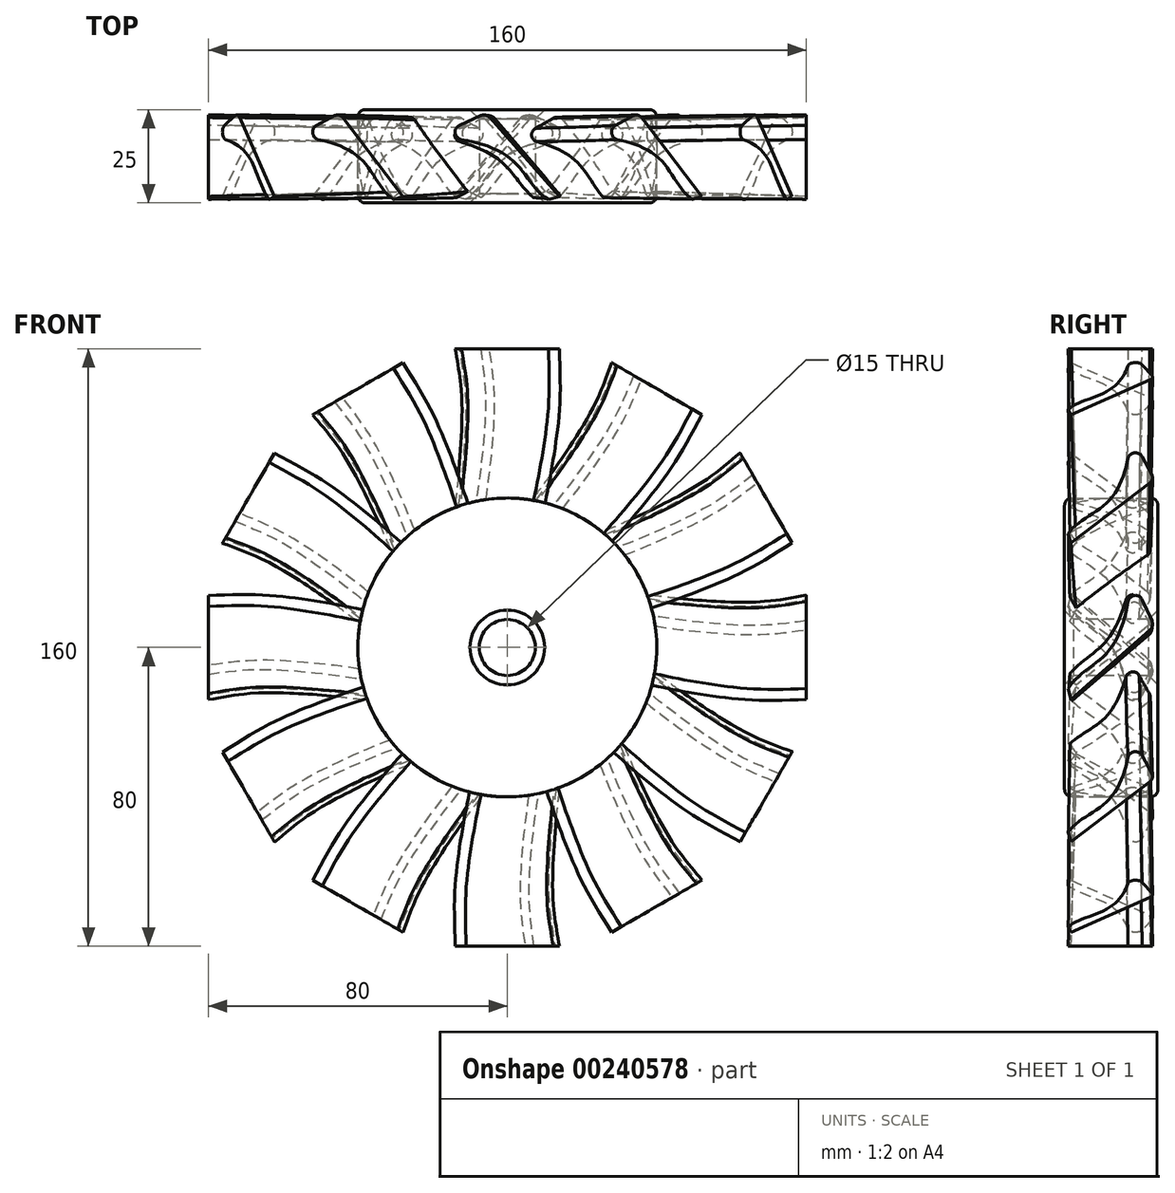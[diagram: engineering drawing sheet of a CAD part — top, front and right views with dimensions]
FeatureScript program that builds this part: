
annotation { "Feature Type Name" : "Feature", "Feature Type Description" : "" }
export const myFeature = defineFeature(function(context is Context, id is Id, definition is map)
    precondition{}
    {
        {
            var Q0;
            Q0=qCreatedBy(makeId("Front.planeOp"),FACE);
            var sketch = newSketch(context, id + "F0", { "sketchPlane" : qUnion([Q0])});
            skCircle(sketch, "E0", {"center": v(0, 0) * mm, "radius": 40 * mm});
            skSolve(sketch);
        }
        {
            var Q0;
            Q0 = qSketchRegion(id + "F0", true);
            extrude(context, id + "F1", {"entities" : qUnion([Q0]), "endBound" : BoundingType.SYMMETRIC, "depth" : 25 * mm});
        }
        {
            var Q0;
            Q0=qCreatedBy(makeId("Right.planeOp"),FACE);
            cPlane(context, id + "F2", {"entities" : qUnion([Q0]), "cplaneType" : CPlaneType.OFFSET, "offset" : 80 * mm, "width" : 150 * mm, "height" : 150 * mm});
        }
        {
            var Q0;
            Q0=qCreatedBy(id+"F2.planeOp",FACE);
            var sketch = newSketch(context, id + "F3", { "sketchPlane" : qUnion([Q0])});
            skLineSegment(sketch, "E1", {"start": v(-11.5, -11) * mm, "end": v(-10.73, -13.9) * mm});
            skLineSegment(sketch, "E2", {"start": v(-10.73, -13.9) * mm, "end": v(11.5, 5.75) * mm});
            skLineSegment(sketch, "E3", {"start": v(11.5, 5.75) * mm, "end": v(5.23, 19.51) * mm});
            skFitSpline(sketch, "E4", {"points": [v(5.23, 19.51) * mm, v(0, 0) * mm, v(-11.5, -11) * mm], "startDerivative": vector(-0.84, -29.08) * mm, "endDerivative": vector(-15.4, -28.23) * mm});
            skSolve(sketch);
        }
        {
            var Q0;
            Q0=qCreatedBy(makeId("Right.planeOp"),FACE);
            var sketch = newSketch(context, id + "F4", { "sketchPlane" : qUnion([Q0])});
            skLineSegment(sketch, "E5", {"start": v(-10.65, 5.34) * mm, "end": v(-8.14, 1.62) * mm});
            skLineSegment(sketch, "E6", {"start": v(-8.14, 1.62) * mm, "end": v(10.63, 16.82) * mm});
            skLineSegment(sketch, "E7", {"start": v(10.63, 16.82) * mm, "end": v(5.11, 23.64) * mm});
            skFitSpline(sketch, "E8", {"points": [v(5.11, 23.64) * mm, v(-1.22, 14) * mm, v(-10.65, 5.34) * mm], "startDerivative": vector(-11.7, -20.48) * mm, "endDerivative": vector(-19.74, -16.14) * mm});
            skSolve(sketch);
        }
        {
            var Q0;
            Q0=qCreatedBy(makeId("Front.planeOp"),FACE);
            var sketch = newSketch(context, id + "F5", { "sketchPlane" : qUnion([Q0])});
            skFitSpline(sketch, "E9", {"points": [v(106.56, 6.15) * mm, v(61.81, -5.32) * mm, v(-7.83, 15.15) * mm], "startDerivative": vector(-74.8, -78.19) * mm, "endDerivative": vector(-107.96, 51.1) * mm});
            skSolve(sketch);
        }
        {
            var Q1;
            Q1=makeQuery(id+"F3.imprint","IMPRINT",FACE,{"disambiguationData":[TD([[makeQuery(id+"F3.imprint","IMPRINT",EDGE,{"derivedFrom":sQuery(id+"F3.wireOp",EDGE,"E1")}),1.0]])]});
            var Q2;
            Q2=makeQuery(id+"F4.imprint","IMPRINT",FACE,{"disambiguationData":[TD([[makeQuery(id+"F4.imprint","IMPRINT",EDGE,{"derivedFrom":sQuery(id+"F4.wireOp",EDGE,"E5")}),1.0]])]});
            var Q3;
            Q3=sQuery(id+"F5.wireOp",EDGE,"E9");
            var Q4;
            Q4=sQuery(id+"F5.wireOp",EDGE,"E9");
            loft(context, id + "F6", {"operationType" : NewBodyOperationType.ADD, "sheetProfilesArray" : [{ "sheetProfileEntities" : qUnion([Q1]) }, { "sheetProfileEntities" : qUnion([Q2]) }], "guidesArray" : [{ "guideEntities" : qUnion([Q3]), "guideDerivativeType" : LoftGuideDerivativeType.DEFAULT, "guideDerivativeMagnitude" : 1 }], "addSections" : true, "spine" : qUnion([Q4]), "sectionCount" : 5});
        }
        {
            var Q0;
            Q0=makeQuery(id+"F6.opLoft","SWEPT_EDGE",EDGE,{"disambiguationData":[OSD([sQuery(id+"F3.wireOp",EDGE,"E3"),sQuery(id+"F3.wireOp",EDGE,"E4"),sQuery(id+"F4.wireOp",EDGE,"E7"),sQuery(id+"F4.wireOp",EDGE,"E8")])]});
            var Q1;
            Q1=makeQuery(id+"F6.opLoft","SWEPT_EDGE",EDGE,{"disambiguationData":[OSD([sQuery(id+"F3.wireOp",EDGE,"E2"),sQuery(id+"F3.wireOp",EDGE,"E3"),sQuery(id+"F4.wireOp",EDGE,"E6"),sQuery(id+"F4.wireOp",EDGE,"E7")])]});
            fillet(context, id + "F7", {"entities" : qUnion([Q0, Q1]), "radius" : 2 * mm, "tangentPropagation" : true, "allowEdgeOverflow" : false});
        }
        {
            var Q0;
            Q0=makeQuery(id+"F1.opExtrude","SWEPT_BODY",BODY,{"disambiguationData":[OSD([sQuery(id+"F0.wireOp",EDGE,"E0")])]});
            var Q1;
            Q1=makeQuery(id+"F1.opExtrude","SWEPT_FACE",FACE,{"disambiguationData":[OSD([sQuery(id+"F0.wireOp",EDGE,"E0")])]});
            circularPattern(context, id + "F8", {"operationType" : NewBodyOperationType.ADD, "entities" : qUnion([Q0]), "axis" : qUnion([Q1]), "angle" : 360 * degree, "instanceCount" : 12, "equalSpace" : true});
        }
        {
            var Q0;
            Q0=qCreatedBy(makeId("Front.planeOp"),FACE);
            var sketch = newSketch(context, id + "F9", { "sketchPlane" : qUnion([Q0])});
            skCircle(sketch, "E10", {"center": v(0, 0) * mm, "radius": 7.5 * mm});
            skSolve(sketch);
        }
        {
            var Q0;
            Q0 = qSketchRegion(id + "F9", true);
            extrude(context, id + "F10", {"entities" : qUnion([Q0]), "operationType" : NewBodyOperationType.REMOVE, "endBound" : BoundingType.THROUGH_ALL, "oppositeDirection" : true, "depth" : 25 * mm, "hasSecondDirection" : true, "secondDirectionBound" : SecondDirectionBoundingType.THROUGH_ALL, "secondDirectionOppositeDirection" : false, "secondDirectionDepth" : 25 * mm});
        }
        {
            var Q0;
            Q0=makeQuery(id+"F10.boolean.opBoolean","INTERSECT",EDGE,{"derivedFrom":[makeQuery(id+"F1.opExtrude","CAP_FACE",FACE,{"disambiguationData":[OSD([sQuery(id+"F0.wireOp",EDGE,"E0")])],"isStart":true}),makeQuery(id+"F10.opExtrude","SWEPT_FACE",FACE,{"disambiguationData":[OSD([sQuery(id+"F9.wireOp",EDGE,"E10")])]})]});
            var Q1;
            Q1=makeQuery(id+"F10.boolean.opBoolean","INTERSECT",EDGE,{"derivedFrom":[makeQuery(id+"F1.opExtrude","CAP_FACE",FACE,{"disambiguationData":[OSD([sQuery(id+"F0.wireOp",EDGE,"E0")])],"isStart":false}),makeQuery(id+"F10.opExtrude","SWEPT_FACE",FACE,{"disambiguationData":[OSD([sQuery(id+"F9.wireOp",EDGE,"E10")])]})]});
            chamfer(context, id + "F11", {"entities" : qUnion([Q0, Q1]), "width" : 2.5 * mm, "tangentPropagation" : true});
        }
        {
            var Q0;
            Q0=makeQuery(id+"F1.opExtrude","CAP_EDGE",EDGE,{"disambiguationData":[OSD([sQuery(id+"F0.wireOp",EDGE,"E0")])],"isStart":true});
            var Q1;
            Q1=makeQuery(id+"F1.opExtrude","CAP_EDGE",EDGE,{"disambiguationData":[OSD([sQuery(id+"F0.wireOp",EDGE,"E0")])],"isStart":false});
            fillet(context, id + "F12", {"entities" : qUnion([Q0, Q1]), "tangentPropagation" : true, "radius" : 2 * mm, "defaultsChanged" : true, "vertexSettings" : [], "allowEdgeOverflow" : false});
        }
    });
